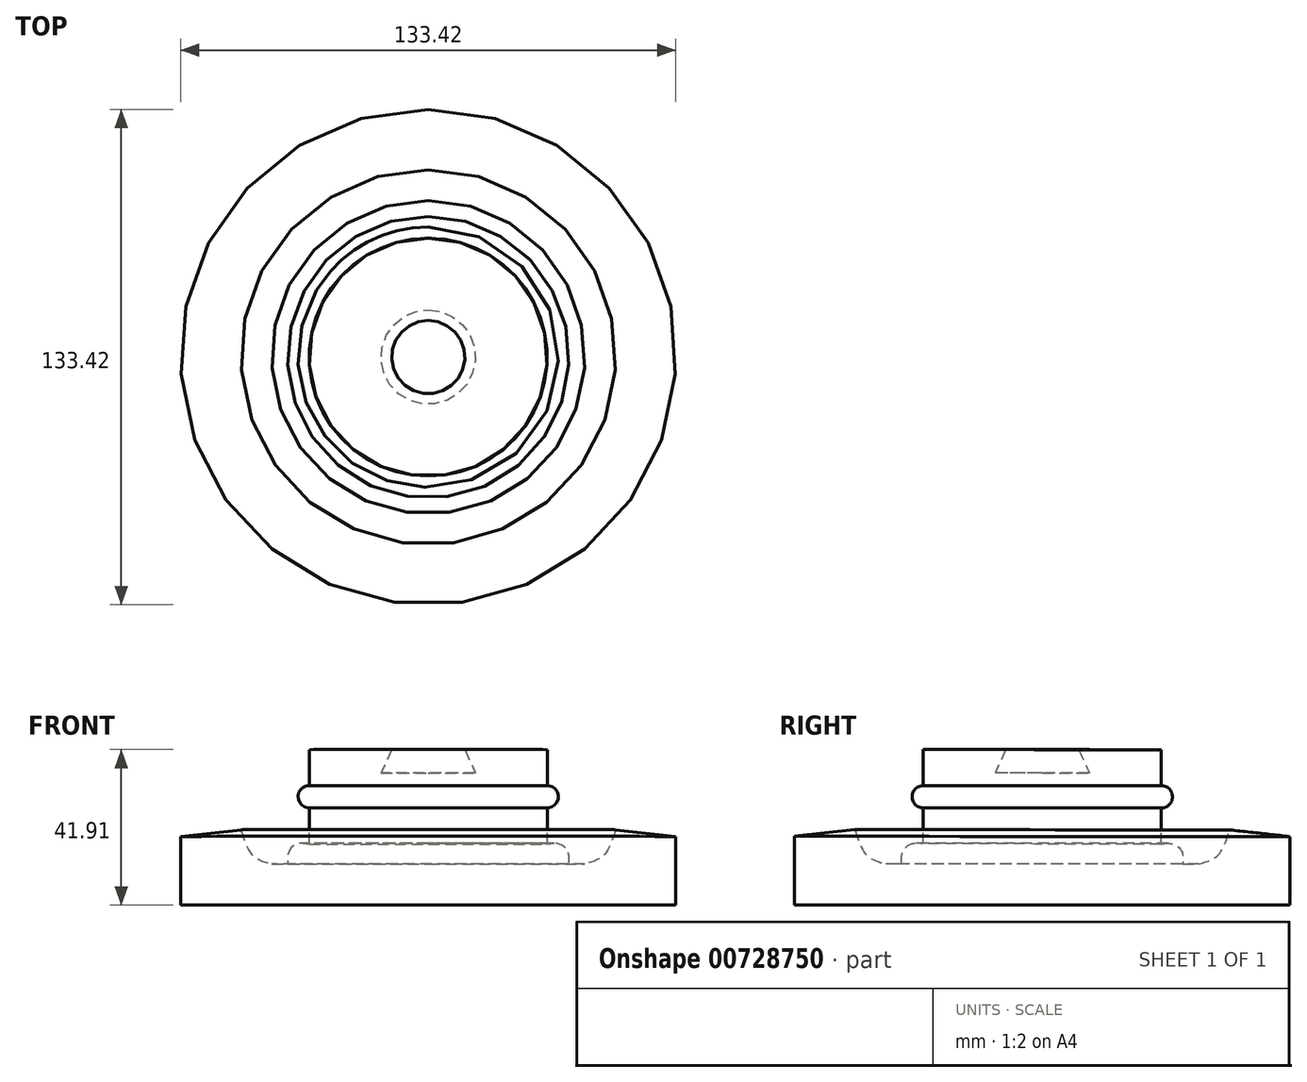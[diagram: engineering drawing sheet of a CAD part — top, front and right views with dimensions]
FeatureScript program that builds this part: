
annotation { "Feature Type Name" : "Feature", "Feature Type Description" : "" }
export const myFeature = defineFeature(function(context is Context, id is Id, definition is map)
    precondition{}
    {
        {
            var Q0;
            Q0=qCreatedBy(makeId("Right.planeOp"),FACE);
            var sketch = newSketch(context, id + "F0", { "sketchPlane" : qUnion([Q0])});
            skLineSegment(sketch, "E0", {"start": v(-69.18, 41.84) * mm, "end": v(-46.96, 41.84) * mm});
            skLineSegment(sketch, "E1", {"start": v(-49.82, 35.49) * mm, "end": v(-46.96, 41.84) * mm});
            skArc(sketch, "E2", {"start": v(-69.18, 26.12) * mm, "mid": v(-72.2, 29.14) * mm, "end": v(-69.18, 32.15) * mm});
            skLineSegment(sketch, "E3", {"start": v(-69.18, 32.15) * mm, "end": v(-69.18, 41.84) * mm});
            skLineSegment(sketch, "E4", {"start": v(-69.18, 26.12) * mm, "end": v(-69.18, 16.44) * mm});
            skPoint(sketch, "E5", {"position": v(-69.18, 35.49) * mm});
            skLineSegment(sketch, "E6", {"start": v(-49.82, 35.49) * mm, "end": v(-37.12, 35.49) * mm});
            skLineSegment(sketch, "E7", {"start": v(-103.83, 0) * mm, "end": v(-37.13, 0) * mm});
            skLineSegment(sketch, "E8", {"start": v(-37.13, 0) * mm, "end": v(-37.12, 35.49) * mm});
            skLineSegment(sketch, "E9", {"start": v(-103.83, 0) * mm, "end": v(-103.83, 18.47) * mm});
            skLineSegment(sketch, "E10", {"start": v(-103.83, 18.47) * mm, "end": v(-87.58, 20.26) * mm});
            skFitSpline(sketch, "E11", {"points": [v(-69.18, 16.44) * mm, v(-72.42, 16.44) * mm, v(-74.72, 14.4) * mm, v(-74.97, 11.08) * mm], "startDerivative": vector(-9.98, 1.46) * mm, "endDerivative": vector(0.78, -10.3) * mm});
            skLineSegment(sketch, "E12", {"start": v(-74.97, 11.08) * mm, "end": v(-79.3, 11.08) * mm});
            skFitSpline(sketch, "E13", {"points": [v(-79.3, 11.08) * mm, v(-84.4, 13.38) * mm, v(-87.58, 20.26) * mm], "startDerivative": vector(-12.21, 3.16) * mm, "endDerivative": vector(-4.54, 14.9) * mm});
            skSolve(sketch);
        }
        {
            var Q0;
            Q0=makeQuery(id+"F0.imprint","IMPRINT",FACE,{"disambiguationData":[TD([[makeQuery(id+"F0.imprint","IMPRINT",EDGE,{"derivedFrom":sQuery(id+"F0.wireOp",EDGE,"E0")}),-1.0]])]});
            var Q1;
            Q1=sQuery(id+"F0.wireOp",EDGE,"E8");
            revolve(context, id + "F1", {"surfaceOperationType" : NewSurfaceOperationType.NEW, "entities" : qUnion([Q0]), "axis" : qUnion([Q1]), "revolveType" : RevolveType.FULL});
        }
    });
